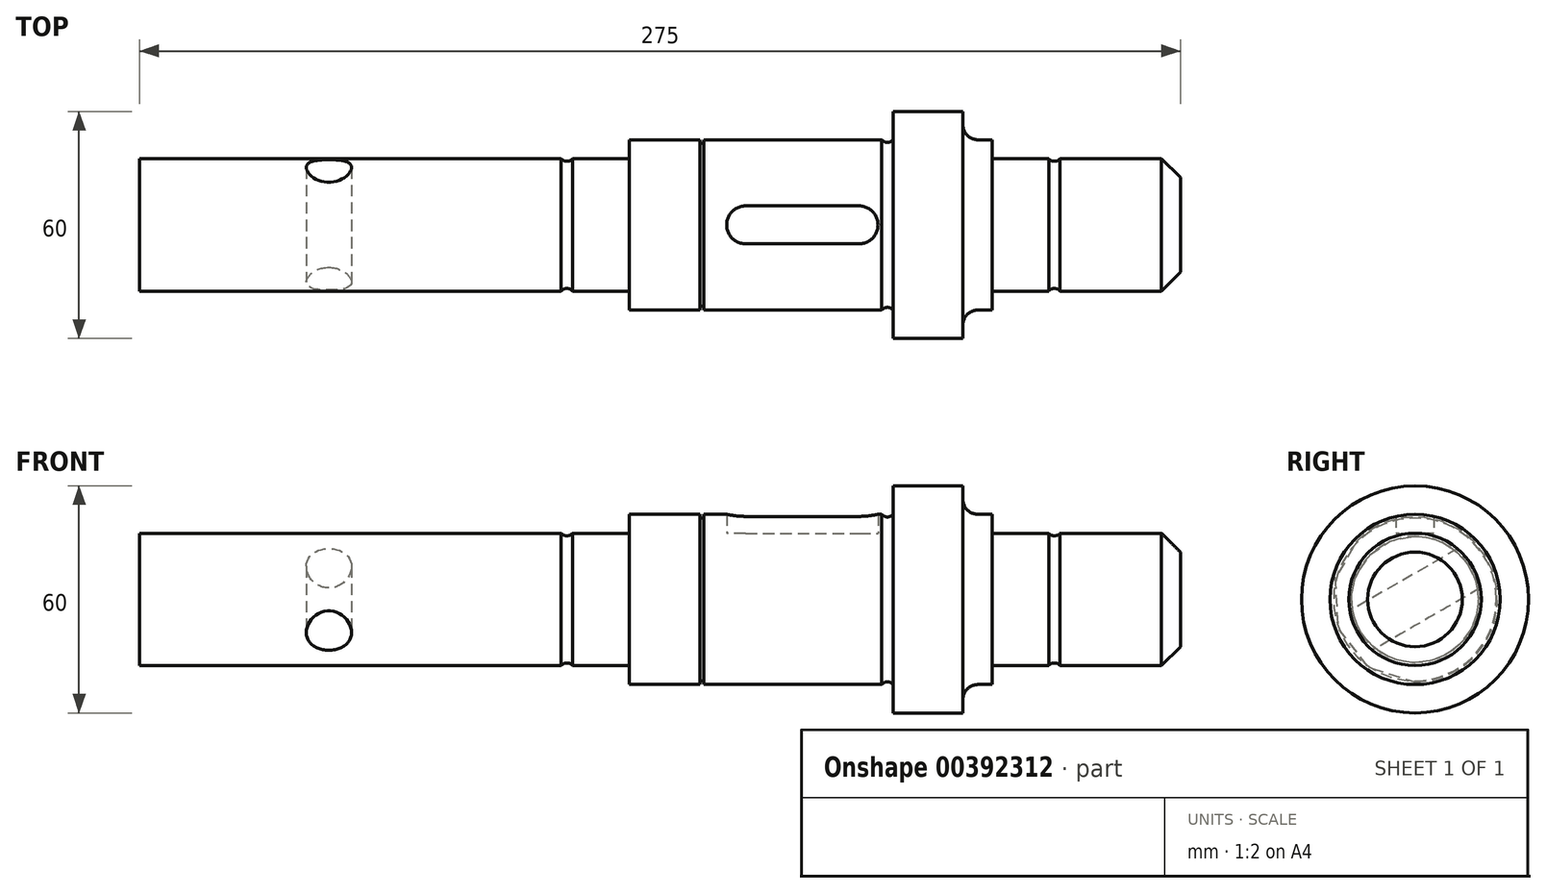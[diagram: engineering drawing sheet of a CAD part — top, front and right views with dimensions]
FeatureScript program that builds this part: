
annotation { "Feature Type Name" : "Feature", "Feature Type Description" : "" }
export const myFeature = defineFeature(function(context is Context, id is Id, definition is map)
    precondition{}
    {
        {
            var Q0;
            Q0=qCreatedBy(makeId("Front.planeOp"),FACE);
            var sketch = newSketch(context, id + "F0", { "sketchPlane" : qUnion([Q0])});
            skLineSegment(sketch, "E0", {"start": v(-207.27, 0) * mm, "end": v(95.62, 0) * mm, "construction": true});
            skLineSegment(sketch, "E1", {"start": v(-199.1, 0) * mm, "end": v(-199.1, 17.5) * mm});
            skLineSegment(sketch, "E2", {"start": v(-199.1, 17.5) * mm, "end": v(-69.7, 17.5) * mm});
            skLineSegment(sketch, "E3", {"start": v(-69.7, 17.5) * mm, "end": v(-69.7, 22.5) * mm});
            skLineSegment(sketch, "E4", {"start": v(-69.7, 22.5) * mm, "end": v(0, 22.5) * mm});
            skLineSegment(sketch, "E5", {"start": v(0, 22.5) * mm, "end": v(0, 30) * mm});
            skLineSegment(sketch, "E6", {"start": v(0, 30) * mm, "end": v(18.4, 30) * mm});
            skLineSegment(sketch, "E7", {"start": v(18.4, 30) * mm, "end": v(18.4, 26.5) * mm});
            skLineSegment(sketch, "E8", {"start": v(22.4, 22.5) * mm, "end": v(26.1, 22.5) * mm});
            skLineSegment(sketch, "E9", {"start": v(26.1, 22.5) * mm, "end": v(26.1, 17.5) * mm});
            skLineSegment(sketch, "E10", {"start": v(26.1, 17.5) * mm, "end": v(70.9, 17.5) * mm});
            skLineSegment(sketch, "E11", {"start": v(75.9, 12.5) * mm, "end": v(75.9, 0) * mm});
            skLineSegment(sketch, "E12", {"start": v(-199.1, 0) * mm, "end": v(75.9, 0) * mm});
            skLineSegment(sketch, "E13", {"start": v(70.9, 17.5) * mm, "end": v(75.9, 12.5) * mm});
            skPoint(sketch, "E14.visualSharp", {"position": v(18.4, 22.5) * mm});
            skArc(sketch, "E14.filletArc", {"start": v(18.4, 26.5) * mm, "mid": v(19.57, 23.67) * mm, "end": v(22.4, 22.5) * mm});
            skSolve(sketch);
        }
        {
            var Q0;
            Q0=qSketchRegion(id+"F0",true);
            var Q1;
            Q1=sQuery(id+"F0.wireOp",EDGE,"E0");
            revolve(context, id + "F1", {"entities" : qUnion([Q0]), "axis" : qUnion([Q1]), "revolveType" : RevolveType.FULL});
        }
        {
            var Q0;
            Q0=qCreatedBy(makeId("Front.planeOp"),FACE);
            var sketch = newSketch(context, id + "F2", { "sketchPlane" : qUnion([Q0])});
            skLineSegment(sketch, "E15.bottom", {"start": v(-51, 33.5) * mm, "end": v(-50, 33.5) * mm});
            skLineSegment(sketch, "E15.top", {"start": v(-51, 21.5) * mm, "end": v(-50, 21.5) * mm});
            skLineSegment(sketch, "E15.left", {"start": v(-51, 33.5) * mm, "end": v(-51, 21.5) * mm});
            skLineSegment(sketch, "E15.right", {"start": v(-50, 33.5) * mm, "end": v(-50, 21.5) * mm});
            skSolve(sketch);
        }
        {
            var Q0;
            Q0=qSketchRegion(id+"F2",true);
            var Q1;
            Q1=sQuery(id+"F0.wireOp",EDGE,"E0");
            revolve(context, id + "F3", {"operationType" : NewBodyOperationType.REMOVE, "entities" : qUnion([Q0]), "axis" : qUnion([Q1]), "revolveType" : RevolveType.FULL, "oppositeDirection" : true});
        }
        {
            var Q0;
            Q0=qCreatedBy(makeId("Front.planeOp"),FACE);
            var sketch = newSketch(context, id + "F4", { "sketchPlane" : qUnion([Q0])});
            skCircle(sketch, "E16", {"center": v(-86.2, 18.76) * mm, "radius": 1.96 * mm});
            skPoint(sketch, "E17", {"position": v(-84.7, 17.5) * mm});
            skPoint(sketch, "E18", {"position": v(-87.7, 17.5) * mm});
            skCircle(sketch, "E19", {"center": v(42.6, 18.76) * mm, "radius": 1.96 * mm});
            skPoint(sketch, "E20", {"position": v(44.1, 17.5) * mm});
            skPoint(sketch, "E21", {"position": v(41.1, 17.5) * mm});
            skArc(sketch, "E22", {"start": v(-3.46, 23.76) * mm, "mid": v(-2.17, 21.92) * mm, "end": v(0, 22.5) * mm});
            skPoint(sketch, "E23", {"position": v(0, 22.5) * mm});
            skPoint(sketch, "E24", {"position": v(-3, 22.5) * mm});
            skLineSegment(sketch, "E25", {"start": v(-3.46, 23.76) * mm, "end": v(-3.46, 32.4) * mm});
            skLineSegment(sketch, "E26", {"start": v(-3.46, 32.4) * mm, "end": v(0, 32.4) * mm});
            skLineSegment(sketch, "E27", {"start": v(0, 32.4) * mm, "end": v(0, 22.5) * mm});
            skSolve(sketch);
        }
        {
            var Q0;
            Q0=qSketchRegion(id+"F4",true);
            var Q1;
            Q1=sQuery(id+"F0.wireOp",EDGE,"E0");
            revolve(context, id + "F5", {"operationType" : NewBodyOperationType.REMOVE, "entities" : qUnion([Q0]), "axis" : qUnion([Q1]), "revolveType" : RevolveType.FULL, "oppositeDirection" : true});
        }
        {
            var Q0;
            Q0=qCreatedBy(makeId("Top.planeOp"),FACE);
            var sketch = newSketch(context, id + "F6", { "sketchPlane" : qUnion([Q0])});
            skArc(sketch, "E28", {"start": v(-39, 5) * mm, "mid": v(-44, 0) * mm, "end": v(-39, -5) * mm});
            skArc(sketch, "E29", {"start": v(-9, -5) * mm, "mid": v(-4, 0) * mm, "end": v(-9, 5) * mm});
            skLineSegment(sketch, "E30", {"start": v(-39, 5) * mm, "end": v(-9, 5) * mm});
            skLineSegment(sketch, "E31", {"start": v(-39, -5) * mm, "end": v(-9, -5) * mm});
            skSolve(sketch);
        }
        {
            var Q0;
            Q0=qSketchRegion(id+"F6",true);
            extrude(context, id + "F7", {"entities" : qUnion([Q0]), "operationType" : NewBodyOperationType.REMOVE, "depth" : 60 * mm, "hasSecondDirection" : true, "secondDirectionOppositeDirection" : false, "secondDirectionDepth" : (45 / 2 - 5) * mm});
        }
        {
            var Q0;
            Q0=qCreatedBy(makeId("Right.planeOp"),FACE);
            cPlane(context, id + "F8", {"entities" : qUnion([Q0]), "cplaneType" : CPlaneType.OFFSET, "offset" : (69.7 + 79.4) * mm, "oppositeDirection" : true, "width" : 150 * mm, "height" : 150 * mm});
        }
        {
            var Q0;
            Q0=qCreatedBy(id+"F8.planeOp",FACE);
            var sketch = newSketch(context, id + "F9", { "sketchPlane" : qUnion([Q0])});
            skLineSegment(sketch, "E32", {"start": v(30.77, 17.76) * mm, "end": v(-51.15, -29.53) * mm, "construction": true});
            skPoint(sketch, "E33", {"position": v(0, 0) * mm});
            skSolve(sketch);
        }
        {
            var Q0;
            Q0=sQuery(id+"F9.wireOp",VERTEX,"E33");
            var Q1;
            Q1=sQuery(id+"F9.wireOp",EDGE,"E32");
            cPlane(context, id + "F10", {"entities" : qUnion([Q0, Q1]), "cplaneType" : CPlaneType.LINE_POINT, "offset" : 25 * mm, "width" : 150 * mm, "height" : 150 * mm});
        }
        {
            var Q0;
            Q0=qCreatedBy(id+"F10.planeOp",FACE);
            var sketch = newSketch(context, id + "F11", { "sketchPlane" : qUnion([Q0])});
            skCircle(sketch, "E34", {"center": v(-149.1, 0) * mm, "radius": 6 * mm});
            skSolve(sketch);
        }
        {
            var Q0;
            Q0=qSketchRegion(id+"F11",true);
            extrude(context, id + "F12", {"entities" : qUnion([Q0]), "operationType" : NewBodyOperationType.REMOVE, "oppositeDirection" : true, "depth" : 25 * mm, "hasSecondDirection" : true, "secondDirectionOppositeDirection" : false, "secondDirectionDepth" : 25 * mm});
        }
    });
